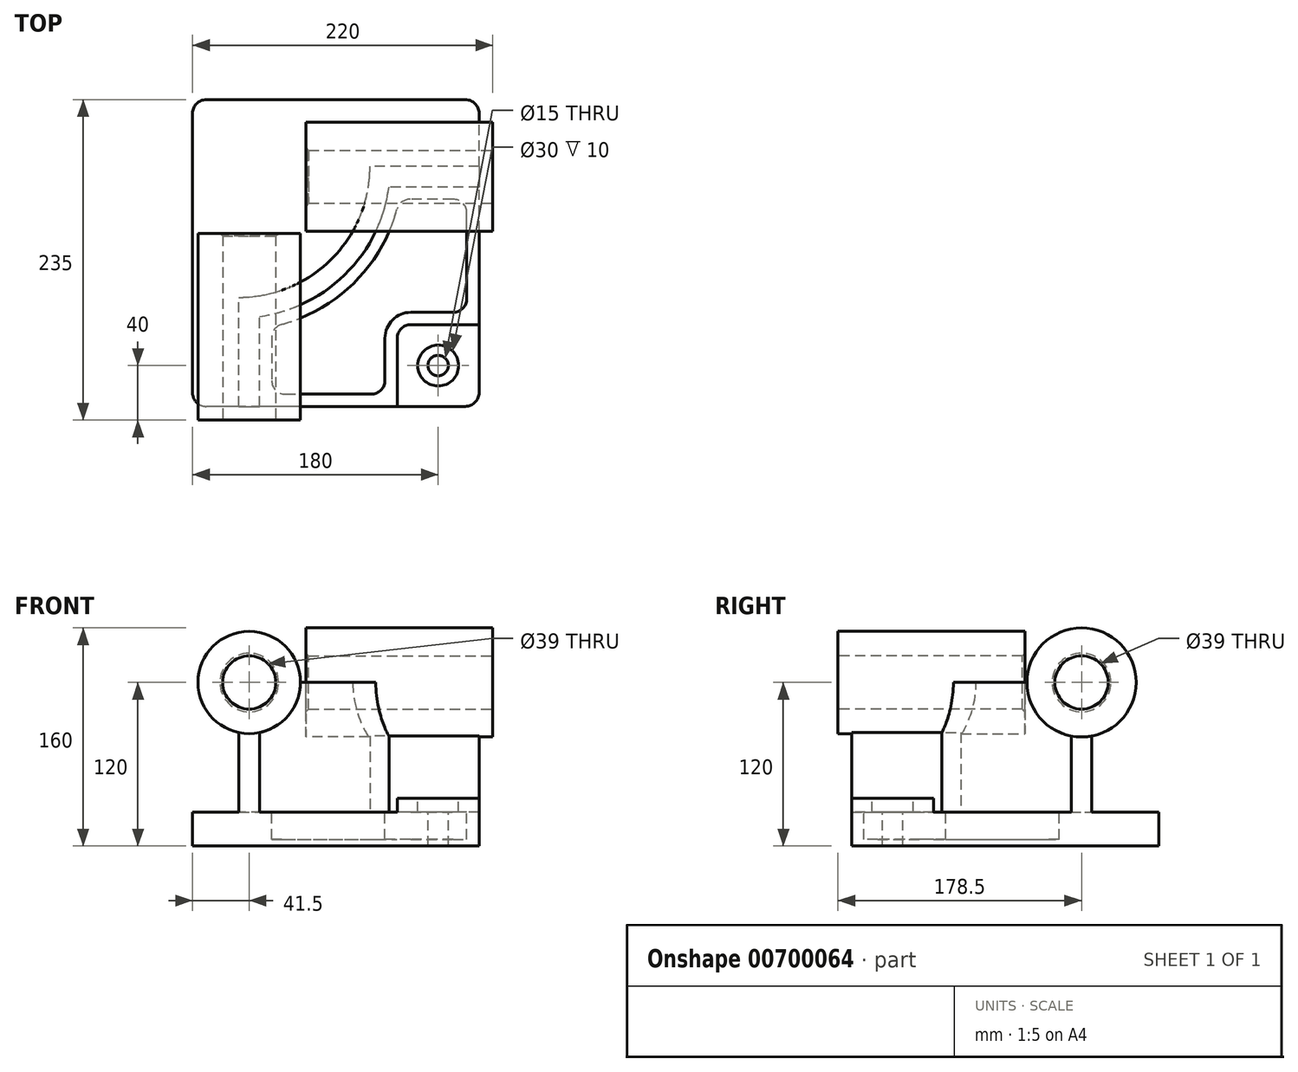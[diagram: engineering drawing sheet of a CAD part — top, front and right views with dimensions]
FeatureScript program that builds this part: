
annotation { "Feature Type Name" : "Feature", "Feature Type Description" : "" }
export const myFeature = defineFeature(function(context is Context, id is Id, definition is map)
    precondition{}
    {
        {
            var Q0;
            Q0=qCreatedBy(makeId("Top.planeOp"),FACE);
            var sketch = newSketch(context, id + "F0", { "sketchPlane" : qUnion([Q0])});
            skLineSegment(sketch, "E0.bottom", {"start": v(105, -112.5) * mm, "end": v(-105, -112.5) * mm});
            skLineSegment(sketch, "E0.top", {"start": v(105, 112.5) * mm, "end": v(-105, 112.5) * mm});
            skLineSegment(sketch, "E0.left", {"start": v(105, -112.5) * mm, "end": v(105, 112.5) * mm});
            skLineSegment(sketch, "E0.right", {"start": v(-105, -112.5) * mm, "end": v(-105, 112.5) * mm});
            skPoint(sketch, "E0.middle", {"position": v(0, 0) * mm});
            skSolve(sketch);
        }
        {
            var Q0;
            Q0=makeQuery(id+"F0.imprint","IMPRINT",FACE,{"disambiguationData":[TD([[makeQuery(id+"F0.imprint","IMPRINT",EDGE,{"derivedFrom":sQuery(id+"F0.wireOp",EDGE,"E0.bottom")}),-1.0]])]});
            extrude(context, id + "F1", {"entities" : qUnion([Q0]), "depth" : 25 * mm, "offsetDistance" : 25 * mm});
        }
        {
            var Q0;
            Q0=makeQuery(id+"F1.opExtrude","CAP_FACE",FACE,{"disambiguationData":[OSD([sQuery(id+"F0.wireOp",EDGE,"E0.bottom"),sQuery(id+"F0.wireOp",EDGE,"E0.top"),sQuery(id+"F0.wireOp",EDGE,"E0.left"),sQuery(id+"F0.wireOp",EDGE,"E0.right")])],"isStart":false});
            var sketch = newSketch(context, id + "F2", { "sketchPlane" : qUnion([Q0])});
            skLineSegment(sketch, "E1", {"start": v(-71, -112.5) * mm, "end": v(-71, -32.5) * mm});
            skLineSegment(sketch, "E2", {"start": v(105, 63.5) * mm, "end": v(25, 63.5) * mm});
            skArc(sketch, "E3", {"start": v(-71, -32.5) * mm, "mid": v(-3.12, -4.38) * mm, "end": v(25, 63.5) * mm});
            skLineSegment(sketch, "E4", {"start": v(-71, 63.5) * mm, "end": v(25, 63.5) * mm, "construction": true});
            skLineSegment(sketch, "E5", {"start": v(-71, 63.5) * mm, "end": v(-71, -32.5) * mm, "construction": true});
            skLineSegment(sketch, "E6.0", {"start": v(-56, -112.5) * mm, "end": v(-56, -46.48) * mm});
            skArc(sketch, "E6.1", {"start": v(-56, -46.48) * mm, "mid": v(7.49, -14.99) * mm, "end": v(38.98, 48.5) * mm});
            skLineSegment(sketch, "E6.2", {"start": v(105, 48.5) * mm, "end": v(38.98, 48.5) * mm});
            skSolve(sketch);
        }
        {
            var Q0;
            {var subQ4=sQuery(id+"F2.wireOp",EDGE,"E1");Q0=makeQuery(id+"F2.imprint","IMPRINT",FACE,{"disambiguationData":[TD([[makeQuery(id+"F2.imprint","IMPRINT",EDGE,{"derivedFrom":subQ4}),-1.0]])]});}
            extrude(context, id + "F3", {"entities" : qUnion([Q0]), "operationType" : NewBodyOperationType.ADD, "depth" : 95 * mm, "offsetDistance" : 25 * mm});
        }
        {
            var Q0;
            {var subQ0=sQuery(id+"F0.wireOp",EDGE,"E0.bottom");Q0=makeQuery(id+"F3.boolean.opBoolean","MERGE",FACE,{"derivedFrom":[makeQuery(id+"F1.opExtrude","SWEPT_FACE",FACE,{"disambiguationData":[OSD([subQ0])]}),makeQuery(id+"F3.opExtrude","SWEPT_FACE",FACE,{"disambiguationData":[OSD([subQ0])]})]});}
            var sketch = newSketch(context, id + "F4", { "sketchPlane" : qUnion([Q0])});
            skCircle(sketch, "E7", {"center": v(-63.5, 120) * mm, "radius": 37.5 * mm});
            skSolve(sketch);
        }
        {
            var Q0;
            Q0 = qSketchRegion(id + "F4", true);
            extrude(context, id + "F5", {"entities" : qUnion([Q0]), "operationType" : NewBodyOperationType.ADD, "depth" : 10 * mm, "offsetDistance" : 25 * mm, "hasSecondDirection" : true, "secondDirectionOppositeDirection" : true, "secondDirectionDepth" : 127 * mm});
        }
        {
            var Q0;
            {var subQ0=sQuery(id+"F0.wireOp",EDGE,"E0.left");Q0=makeQuery(id+"F3.boolean.opBoolean","MERGE",FACE,{"derivedFrom":[makeQuery(id+"F1.opExtrude","SWEPT_FACE",FACE,{"disambiguationData":[OSD([subQ0])]}),makeQuery(id+"F3.opExtrude","SWEPT_FACE",FACE,{"disambiguationData":[OSD([subQ0])]})]});}
            var sketch = newSketch(context, id + "F6", { "sketchPlane" : qUnion([Q0])});
            skCircle(sketch, "E8", {"center": v(56, 120) * mm, "radius": 40 * mm});
            skSolve(sketch);
        }
        {
            var Q0;
            Q0 = qSketchRegion(id + "F6", true);
            extrude(context, id + "F7", {"entities" : qUnion([Q0]), "operationType" : NewBodyOperationType.ADD, "depth" : 10 * mm, "offsetDistance" : 25 * mm, "hasSecondDirection" : true, "secondDirectionOppositeDirection" : true, "secondDirectionDepth" : 127 * mm});
        }
        {
            var Q0;
            {var subQ0=sQuery(id+"F0.wireOp",EDGE,"E0.left");var subQ1=sQuery(id+"F0.wireOp",EDGE,"E0.bottom");Q0=makeQuery(id+"F3.boolean.opBoolean","SPLIT",FACE,{"disambiguationData":[TD([makeQuery(id+"F3.opExtrude","SWEPT_FACE",FACE,{"disambiguationData":[OSD([sQuery(id+"F2.wireOp",EDGE,"E6.0")])]})])],"derivedFrom":makeQuery(id+"F1.opExtrude","CAP_FACE",FACE,{"disambiguationData":[OSD([subQ1,sQuery(id+"F0.wireOp",EDGE,"E0.top"),subQ0,sQuery(id+"F0.wireOp",EDGE,"E0.right")])],"isStart":false})});}
            var sketch = newSketch(context, id + "F8", { "sketchPlane" : qUnion([Q0])});
            skLineSegment(sketch, "E9.bottom", {"start": v(105, -112.5) * mm, "end": v(45, -112.5) * mm});
            skLineSegment(sketch, "E9.top", {"start": v(105, -52.5) * mm, "end": v(45, -52.5) * mm});
            skLineSegment(sketch, "E9.left", {"start": v(105, -112.5) * mm, "end": v(105, -52.5) * mm});
            skLineSegment(sketch, "E9.right", {"start": v(45, -112.5) * mm, "end": v(45, -52.5) * mm});
            skSolve(sketch);
        }
        {
            var Q0;
            Q0 = qSketchRegion(id + "F8", true);
            extrude(context, id + "F9", {"entities" : qUnion([Q0]), "operationType" : NewBodyOperationType.ADD, "depth" : 10 * mm, "offsetDistance" : 25 * mm});
        }
        {
            var Q0;
            Q0=makeQuery(id+"F9.opExtrude","SWEPT_EDGE",EDGE,{"disambiguationData":[OSD([sQuery(id+"F8.wireOp",EDGE,"E9.top"),sQuery(id+"F8.wireOp",EDGE,"E9.right")])]});
            fillet(context, id + "F10", {"entities" : qUnion([Q0]), "radius" : 10 * mm, "tangentPropagation" : true, "allowEdgeOverflow" : false});
        }
        {
            var Q0;
            {var subQ0=sQuery(id+"F0.wireOp",EDGE,"E0.left");var subQ1=sQuery(id+"F0.wireOp",EDGE,"E0.bottom");Q0=makeQuery(id+"F3.boolean.opBoolean","SPLIT",FACE,{"disambiguationData":[TD([makeQuery(id+"F3.opExtrude","SWEPT_FACE",FACE,{"disambiguationData":[OSD([sQuery(id+"F2.wireOp",EDGE,"E6.0")])]})])],"derivedFrom":makeQuery(id+"F1.opExtrude","CAP_FACE",FACE,{"disambiguationData":[OSD([subQ1,sQuery(id+"F0.wireOp",EDGE,"E0.top"),subQ0,sQuery(id+"F0.wireOp",EDGE,"E0.right")])],"isStart":false})});}
            var sketch = newSketch(context, id + "F11", { "sketchPlane" : qUnion([Q0])});
            skLineSegment(sketch, "E10.0", {"start": v(-47, -54.08) * mm, "end": v(-47, -103.5) * mm});
            skArc(sketch, "E10.1", {"start": v(46.58, 39.5) * mm, "mid": v(13.85, -21.35) * mm, "end": v(-47, -54.08) * mm});
            skLineSegment(sketch, "E10.2", {"start": v(-47, -103.5) * mm, "end": v(36, -103.5) * mm});
            skLineSegment(sketch, "E10.3", {"start": v(96, 39.5) * mm, "end": v(46.58, 39.5) * mm});
            skLineSegment(sketch, "E10.4", {"start": v(36, -103.5) * mm, "end": v(36, -62.5) * mm});
            skArc(sketch, "E10.5", {"start": v(36, -62.5) * mm, "mid": v(41.56, -49.06) * mm, "end": v(55, -43.5) * mm});
            skLineSegment(sketch, "E10.6", {"start": v(55, -43.5) * mm, "end": v(96, -43.5) * mm});
            skLineSegment(sketch, "E10.7", {"start": v(96, -43.5) * mm, "end": v(96, 39.5) * mm});
            skSolve(sketch);
        }
        {
            var Q0;
            Q0 = qSketchRegion(id + "F11", true);
            extrude(context, id + "F12", {"entities" : qUnion([Q0]), "operationType" : NewBodyOperationType.REMOVE, "oppositeDirection" : true, "depth" : 20 * mm, "offsetDistance" : 25 * mm});
        }
        {
            var Q0;
            Q0=makeQuery(id+"F9.opExtrude","CAP_FACE",FACE,{"disambiguationData":[OSD([sQuery(id+"F8.wireOp",EDGE,"E9.bottom"),sQuery(id+"F8.wireOp",EDGE,"E9.top"),sQuery(id+"F8.wireOp",EDGE,"E9.left"),sQuery(id+"F8.wireOp",EDGE,"E9.right")])],"isStart":false});
            var sketch = newSketch(context, id + "F13", { "sketchPlane" : qUnion([Q0])});
            skCircle(sketch, "E11", {"center": v(75, -82.5) * mm, "radius": 15 * mm});
            skSolve(sketch);
        }
        {
            var Q0;
            Q0=sQuery(id+"F13.wireOp",VERTEX,"E11.center");
            var Q1;
            Q1=makeQuery(id+"F1.opExtrude","SWEPT_BODY",BODY,{"disambiguationData":[OSD([sQuery(id+"F0.wireOp",EDGE,"E0.bottom"),sQuery(id+"F0.wireOp",EDGE,"E0.top"),sQuery(id+"F0.wireOp",EDGE,"E0.left"),sQuery(id+"F0.wireOp",EDGE,"E0.right")])]});
            hole(context, id + "F14", {"style" : HoleStyle.C_BORE, "endStyle" : HoleEndStyle.THROUGH, "holeDiameter" : 15 * mm, "cBoreDiameter" : 30 * mm, "cBoreDepth" : 10 * mm, "majorDiameter" : 5 * mm, "isTappedThrough" : true, "tappedDepth" : 12 * mm, "tapClearance" : 3, "locations" : qUnion([Q0]), "scope" : qUnion([Q1])});
        }
        {
            var Q0;
            Q0=makeQuery(id+"F12.boolean.opBoolean","COPY",EDGE,{"derivedFrom":makeQuery(id+"F12.opExtrude","SWEPT_EDGE",EDGE,{"disambiguationData":[OSD([sQuery(id+"F11.wireOp",EDGE,"E10.0"),sQuery(id+"F11.wireOp",EDGE,"E10.1")])]})});
            var Q1;
            Q1=makeQuery(id+"F12.boolean.opBoolean","COPY",EDGE,{"derivedFrom":makeQuery(id+"F12.opExtrude","SWEPT_EDGE",EDGE,{"disambiguationData":[OSD([sQuery(id+"F11.wireOp",EDGE,"E10.1"),sQuery(id+"F11.wireOp",EDGE,"E10.3")])]})});
            var Q2;
            Q2=makeQuery(id+"F12.boolean.opBoolean","COPY",EDGE,{"derivedFrom":makeQuery(id+"F12.opExtrude","SWEPT_EDGE",EDGE,{"disambiguationData":[OSD([sQuery(id+"F11.wireOp",EDGE,"E10.3"),sQuery(id+"F11.wireOp",EDGE,"E10.7")])]})});
            var Q3;
            Q3=makeQuery(id+"F12.boolean.opBoolean","COPY",EDGE,{"derivedFrom":makeQuery(id+"F12.opExtrude","SWEPT_EDGE",EDGE,{"disambiguationData":[OSD([sQuery(id+"F11.wireOp",EDGE,"E10.0"),sQuery(id+"F11.wireOp",EDGE,"E10.2")])]})});
            var Q4;
            Q4=makeQuery(id+"F12.boolean.opBoolean","COPY",EDGE,{"derivedFrom":makeQuery(id+"F12.opExtrude","SWEPT_EDGE",EDGE,{"disambiguationData":[OSD([sQuery(id+"F11.wireOp",EDGE,"E10.2"),sQuery(id+"F11.wireOp",EDGE,"E10.4")])]})});
            var Q5;
            Q5=makeQuery(id+"F12.boolean.opBoolean","COPY",EDGE,{"derivedFrom":makeQuery(id+"F12.opExtrude","SWEPT_EDGE",EDGE,{"disambiguationData":[OSD([sQuery(id+"F11.wireOp",EDGE,"E10.6"),sQuery(id+"F11.wireOp",EDGE,"E10.7")])]})});
            fillet(context, id + "F15", {"entities" : qUnion([Q0, Q1, Q2, Q3, Q4, Q5]), "radius" : 10 * mm, "tangentPropagation" : true, "allowEdgeOverflow" : false});
        }
        {
            var Q0;
            Q0=makeQuery(id+"F5.opExtrude","CAP_FACE",FACE,{"disambiguationData":[OSD([sQuery(id+"F4.wireOp",EDGE,"E7")])],"isStart":false});
            var sketch = newSketch(context, id + "F16", { "sketchPlane" : qUnion([Q0])});
            skCircle(sketch, "E12", {"center": v(-63.5, 120) * mm, "radius": 19.5 * mm});
            skSolve(sketch);
        }
        {
            var Q0;
            Q0 = qSketchRegion(id + "F16", true);
            extrude(context, id + "F17", {"entities" : qUnion([Q0]), "operationType" : NewBodyOperationType.REMOVE, "endBound" : BoundingType.THROUGH_ALL, "oppositeDirection" : true, "depth" : 25 * mm, "offsetDistance" : 25 * mm});
        }
        {
            var Q0;
            Q0=makeQuery(id+"F7.opExtrude","CAP_FACE",FACE,{"disambiguationData":[OSD([sQuery(id+"F6.wireOp",EDGE,"E8")])],"isStart":false});
            var sketch = newSketch(context, id + "F18", { "sketchPlane" : qUnion([Q0])});
            skCircle(sketch, "E13", {"center": v(56, 120) * mm, "radius": 19.5 * mm});
            skSolve(sketch);
        }
        {
            var Q0;
            Q0 = qSketchRegion(id + "F18", true);
            extrude(context, id + "F19", {"entities" : qUnion([Q0]), "operationType" : NewBodyOperationType.REMOVE, "endBound" : BoundingType.THROUGH_ALL, "oppositeDirection" : true, "depth" : 25 * mm, "offsetDistance" : 25 * mm});
        }
        {
            var Q0;
            Q0=makeQuery(id+"F17.boolean.opBoolean","COPY",EDGE,{"derivedFrom":makeQuery(id+"F17.opExtrude","CAP_EDGE",EDGE,{"disambiguationData":[OSD([sQuery(id+"F16.wireOp",EDGE,"E12")])],"isStart":true})});
            var Q1;
            Q1=makeQuery(id+"F19.boolean.opBoolean","COPY",EDGE,{"derivedFrom":makeQuery(id+"F19.opExtrude","CAP_EDGE",EDGE,{"disambiguationData":[OSD([sQuery(id+"F18.wireOp",EDGE,"E13")])],"isStart":true})});
            var Q2;
            Q2=makeQuery(id+"F19.boolean.opBoolean","INTERSECT",EDGE,{"derivedFrom":[makeQuery(id+"F7.opExtrude","CAP_FACE",FACE,{"disambiguationData":[OSD([sQuery(id+"F6.wireOp",EDGE,"E8")])],"isStart":true}),makeQuery(id+"F19.opExtrude","SWEPT_FACE",FACE,{"disambiguationData":[OSD([sQuery(id+"F18.wireOp",EDGE,"E13")])]})]});
            var Q3;
            Q3=makeQuery(id+"F17.boolean.opBoolean","INTERSECT",EDGE,{"derivedFrom":[makeQuery(id+"F5.opExtrude","CAP_FACE",FACE,{"disambiguationData":[OSD([sQuery(id+"F4.wireOp",EDGE,"E7")])],"isStart":true}),makeQuery(id+"F17.opExtrude","SWEPT_FACE",FACE,{"disambiguationData":[OSD([sQuery(id+"F16.wireOp",EDGE,"E12")])]})]});
            chamfer(context, id + "F20", {"entities" : qUnion([Q0, Q1, Q2, Q3]), "width" : 2 * mm, "tangentPropagation" : true});
        }
        {
            var Q0;
            Q0=makeQuery(id+"F9.boolean.opBoolean","MERGE",EDGE,{"derivedFrom":[makeQuery(id+"F1.opExtrude","SWEPT_EDGE",EDGE,{"disambiguationData":[OSD([sQuery(id+"F0.wireOp",EDGE,"E0.bottom"),sQuery(id+"F0.wireOp",EDGE,"E0.left")])]}),makeQuery(id+"F9.opExtrude","SWEPT_EDGE",EDGE,{"disambiguationData":[OSD([sQuery(id+"F8.wireOp",EDGE,"E9.bottom"),sQuery(id+"F8.wireOp",EDGE,"E9.left")])]})]});
            var Q1;
            Q1=makeQuery(id+"F1.opExtrude","SWEPT_EDGE",EDGE,{"disambiguationData":[OSD([sQuery(id+"F0.wireOp",EDGE,"E0.top"),sQuery(id+"F0.wireOp",EDGE,"E0.left")])]});
            var Q2;
            Q2=makeQuery(id+"F1.opExtrude","SWEPT_EDGE",EDGE,{"disambiguationData":[OSD([sQuery(id+"F0.wireOp",EDGE,"E0.bottom"),sQuery(id+"F0.wireOp",EDGE,"E0.right")])]});
            var Q3;
            Q3=makeQuery(id+"F1.opExtrude","SWEPT_EDGE",EDGE,{"disambiguationData":[OSD([sQuery(id+"F0.wireOp",EDGE,"E0.top"),sQuery(id+"F0.wireOp",EDGE,"E0.right")])]});
            fillet(context, id + "F21", {"entities" : qUnion([Q0, Q1, Q2, Q3]), "radius" : 10 * mm, "tangentPropagation" : true, "allowEdgeOverflow" : false});
        }
    });
